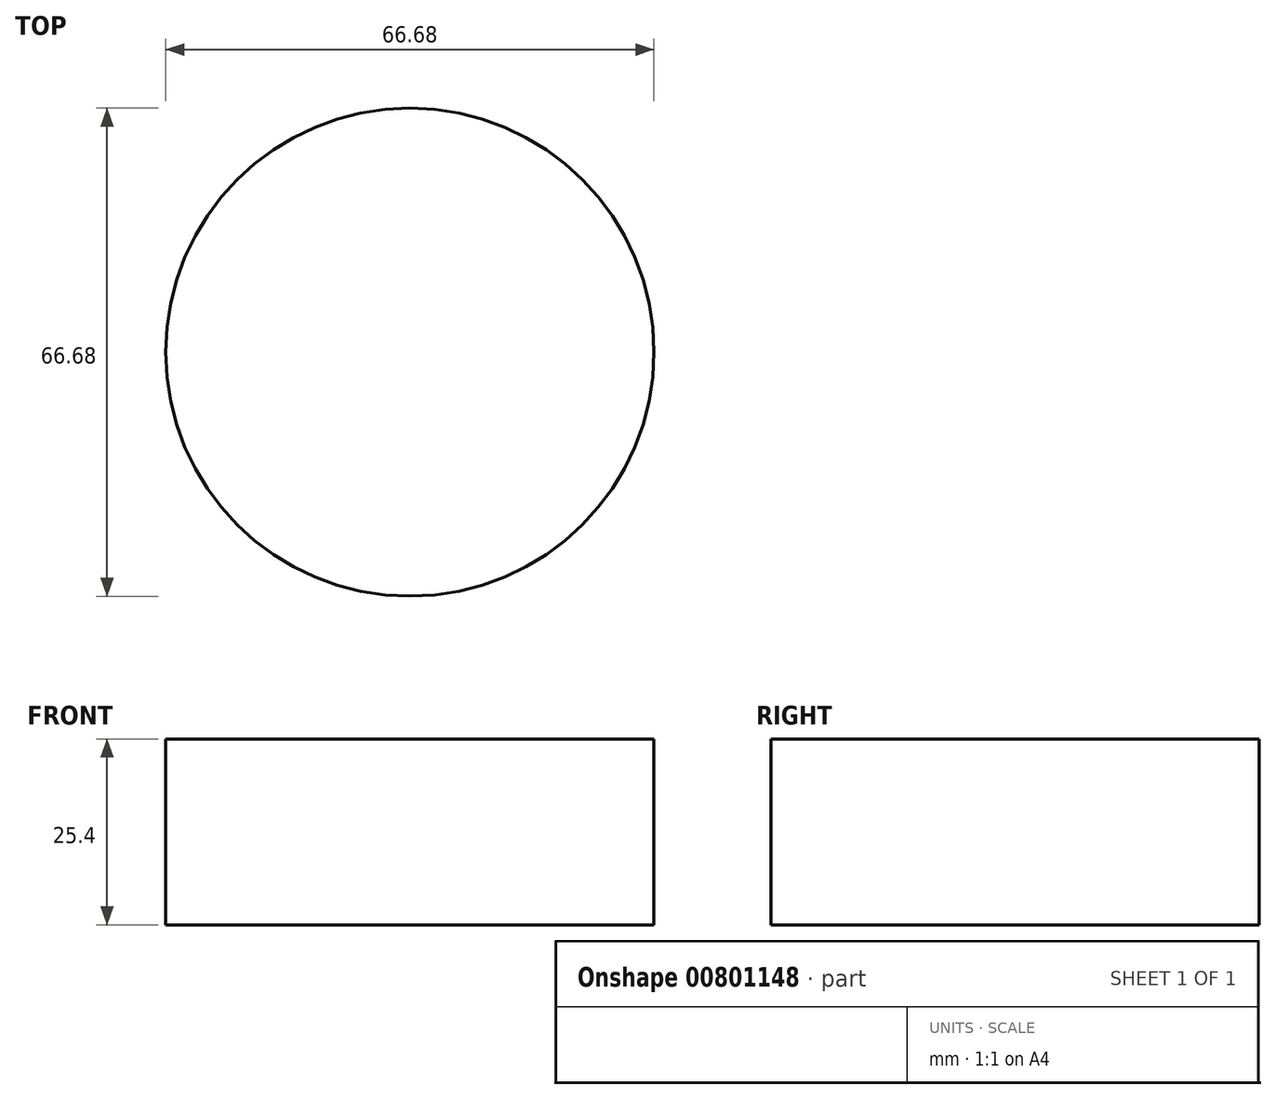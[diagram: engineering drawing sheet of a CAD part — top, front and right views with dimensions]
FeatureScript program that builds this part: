
annotation { "Feature Type Name" : "Feature", "Feature Type Description" : "" }
export const myFeature = defineFeature(function(context is Context, id is Id, definition is map)
    precondition{}
    {
        {
            var Q0;
            Q0=qCreatedBy(makeId("Top.planeOp"),FACE);
            var sketch = newSketch(context, id + "F0", { "sketchPlane" : qUnion([Q0])});
            skCircle(sketch, "E0", {"center": v(0, 0) * mm, "radius": 33.34 * mm});
            skSolve(sketch);
        }
        {
            var Q0;
            Q0=makeQuery(id+"F0.imprint","IMPRINT",FACE,{"disambiguationData":[TD([[makeQuery(id+"F0.imprint","IMPRINT",EDGE,{"derivedFrom":sQuery(id+"F0.wireOp",EDGE,"E0")}),1.0]])]});
            extrude(context, id + "F1", {"entities" : qUnion([Q0]), "depth" : 25.4 * mm, "offsetDistance" : 25.4 * mm});
        }
    });
